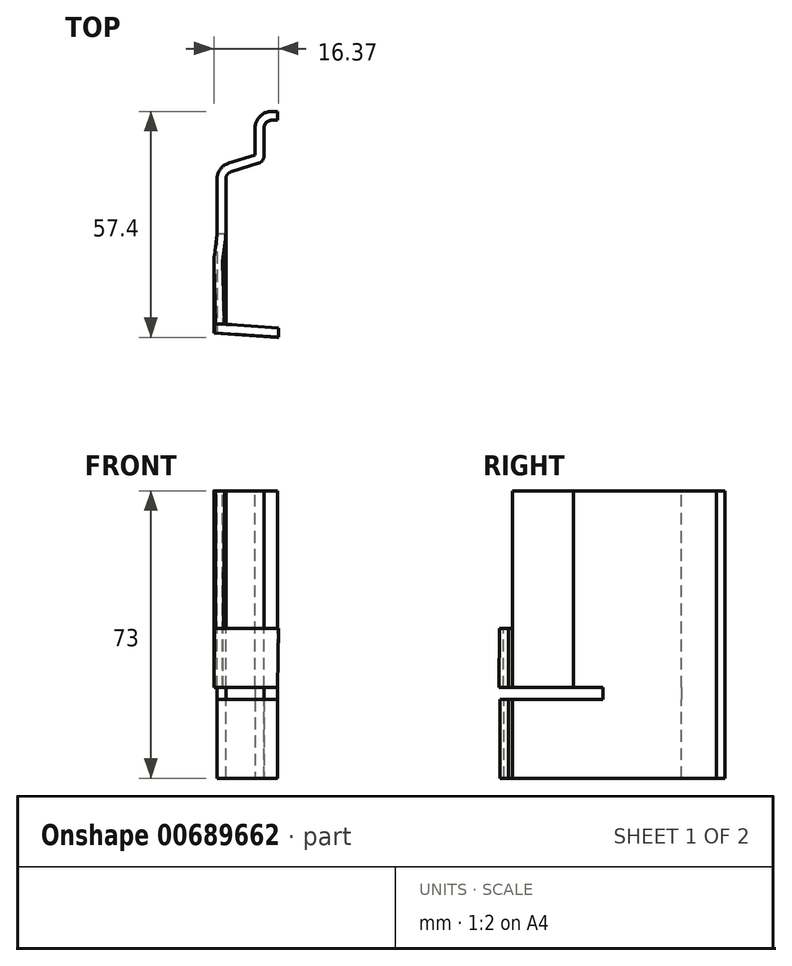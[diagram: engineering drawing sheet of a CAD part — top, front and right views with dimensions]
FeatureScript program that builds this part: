
annotation { "Feature Type Name" : "Feature", "Feature Type Description" : "" }
export const myFeature = defineFeature(function(context is Context, id is Id, definition is map)
    precondition{}
    {
        {
            var Q0;
            Q0=qCreatedBy(makeId("Top.planeOp"),FACE);
            var sketch = newSketch(context, id + "F0", { "sketchPlane" : qUnion([Q0])});
            skLineSegment(sketch, "E0", {"start": v(-3.5, 27.5) * mm, "end": v(-3.5, 20.47) * mm});
            skLineSegment(sketch, "E1", {"start": v(-4.9, 18.56) * mm, "end": v(-11.8, 16.44) * mm});
            skLineSegment(sketch, "E2", {"start": v(-13.2, 14.53) * mm, "end": v(-13.2, 0.66) * mm});
            skLineSegment(sketch, "E3", {"start": v(-13.29, -0.66) * mm, "end": v(-13.9, -5.19) * mm});
            skLineSegment(sketch, "E4", {"start": v(-13.97, -6.82) * mm, "end": v(-13.5, -22.25) * mm});
            skLineSegment(sketch, "E5", {"start": v(-1.5, 29.5) * mm, "end": v(0, 29.5) * mm});
            skPoint(sketch, "E6.visualSharp", {"position": v(-13.2, 16) * mm});
            skArc(sketch, "E6.filletArc", {"start": v(-11.8, 16.44) * mm, "mid": v(-12.8, 15.71) * mm, "end": v(-13.2, 14.53) * mm});
            skPoint(sketch, "E7.visualSharp", {"position": v(-3.5, 19) * mm});
            skArc(sketch, "E7.filletArc", {"start": v(-4.9, 18.56) * mm, "mid": v(-3.9, 19.29) * mm, "end": v(-3.5, 20.47) * mm});
            skPoint(sketch, "E8.visualSharp", {"position": v(-3.5, 29.5) * mm});
            skArc(sketch, "E8.filletArc", {"start": v(-1.5, 29.5) * mm, "mid": v(-2.91, 28.91) * mm, "end": v(-3.5, 27.5) * mm});
            skPoint(sketch, "E9.visualSharp", {"position": v(-13.2, 0) * mm});
            skArc(sketch, "E9.filletArc", {"start": v(-13.29, -0.66) * mm, "mid": v(-13.22, 0) * mm, "end": v(-13.2, 0.66) * mm});
            skPoint(sketch, "E10.visualSharp", {"position": v(-14, -6) * mm});
            skArc(sketch, "E10.filletArc", {"start": v(-13.9, -5.19) * mm, "mid": v(-13.97, -6) * mm, "end": v(-13.97, -6.82) * mm});
            skLineSegment(sketch, "E11.0", {"start": v(-16.22, -6.89) * mm, "end": v(-15.75, -22.32) * mm});
            skArc(sketch, "E11.1", {"start": v(-16.12, -4.9) * mm, "mid": v(-16.21, -5.89) * mm, "end": v(-16.22, -6.89) * mm});
            skLineSegment(sketch, "E11.2", {"start": v(-15.52, -0.36) * mm, "end": v(-16.12, -4.9) * mm});
            skArc(sketch, "E11.3", {"start": v(-15.52, -0.36) * mm, "mid": v(-15.47, 0.15) * mm, "end": v(-15.45, 0.66) * mm});
            skLineSegment(sketch, "E11.4", {"start": v(-15.45, 14.53) * mm, "end": v(-15.45, 0.66) * mm});
            skArc(sketch, "E11.5", {"start": v(-12.46, 18.59) * mm, "mid": v(-14.62, 17.05) * mm, "end": v(-15.45, 14.53) * mm});
            skLineSegment(sketch, "E11.6", {"start": v(-1.5, 31.75) * mm, "end": v(0, 31.75) * mm});
            skArc(sketch, "E11.7", {"start": v(-1.5, 31.75) * mm, "mid": v(-4.5, 30.5) * mm, "end": v(-5.75, 27.5) * mm});
            skLineSegment(sketch, "E11.8", {"start": v(-5.75, 27.5) * mm, "end": v(-5.75, 20.66) * mm});
            skLineSegment(sketch, "E11.9", {"start": v(-5.75, 20.66) * mm, "end": v(-12.46, 18.59) * mm});
            skLineSegment(sketch, "E12", {"start": v(-13.5, -22.25) * mm, "end": v(-15.75, -22.32) * mm});
            skLineSegment(sketch, "E13", {"start": v(0, 29.5) * mm, "end": v(0, 31.75) * mm});
            skSolve(sketch);
        }
        {
            var Q0;
            Q0=qCreatedBy(makeId("Top.planeOp"),FACE);
            cPlane(context, id + "F1", {"entities" : qUnion([Q0]), "cplaneType" : CPlaneType.OFFSET, "offset" : 50 * mm, "oppositeDirection" : true, "width" : 150 * mm, "height" : 150 * mm});
        }
        {
            var Q0;
            Q0=qCreatedBy(id+"F1.planeOp",FACE);
            var sketch = newSketch(context, id + "F2", { "sketchPlane" : qUnion([Q0])});
            skLineSegment(sketch, "E14", {"start": v(-3.5, 27.5) * mm, "end": v(-3.5, 20.47) * mm});
            skLineSegment(sketch, "E15", {"start": v(-4.9, 18.56) * mm, "end": v(-11.8, 16.44) * mm});
            skLineSegment(sketch, "E16", {"start": v(-13.2, 14.53) * mm, "end": v(-13.2, 0.66) * mm});
            skLineSegment(sketch, "E17", {"start": v(-13.29, -0.66) * mm, "end": v(-13.9, -5.19) * mm});
            skLineSegment(sketch, "E18", {"start": v(-1.5, 29.5) * mm, "end": v(0, 29.5) * mm});
            skPoint(sketch, "E19.visualSharp", {"position": v(-13.2, 16) * mm});
            skArc(sketch, "E19.filletArc", {"start": v(-11.8, 16.44) * mm, "mid": v(-12.8, 15.71) * mm, "end": v(-13.2, 14.53) * mm});
            skPoint(sketch, "E20.visualSharp", {"position": v(-3.5, 19) * mm});
            skArc(sketch, "E20.filletArc", {"start": v(-4.9, 18.56) * mm, "mid": v(-3.9, 19.29) * mm, "end": v(-3.5, 20.47) * mm});
            skPoint(sketch, "E21.visualSharp", {"position": v(-3.5, 29.5) * mm});
            skArc(sketch, "E21.filletArc", {"start": v(-1.5, 29.5) * mm, "mid": v(-2.91, 28.91) * mm, "end": v(-3.5, 27.5) * mm});
            skPoint(sketch, "E22.visualSharp", {"position": v(-13.2, 0) * mm});
            skArc(sketch, "E22.filletArc", {"start": v(-13.29, -0.66) * mm, "mid": v(-13.22, 0) * mm, "end": v(-13.2, 0.66) * mm});
            skPoint(sketch, "E23.visualSharp", {"position": v(-14, -6) * mm});
            skArc(sketch, "E23.filletArc", {"start": v(-13.9, -5.19) * mm, "mid": v(-13.97, -6) * mm, "end": v(-13.97, -6.82) * mm});
            skArc(sketch, "E24.1", {"start": v(-16.12, -4.9) * mm, "mid": v(-16.21, -5.89) * mm, "end": v(-16.22, -6.89) * mm});
            skLineSegment(sketch, "E24.2", {"start": v(-15.52, -0.36) * mm, "end": v(-16.12, -4.9) * mm});
            skArc(sketch, "E24.3", {"start": v(-15.52, -0.36) * mm, "mid": v(-15.47, 0.15) * mm, "end": v(-15.45, 0.66) * mm});
            skLineSegment(sketch, "E24.4", {"start": v(-15.45, 14.53) * mm, "end": v(-15.45, 0.66) * mm});
            skArc(sketch, "E24.5", {"start": v(-12.46, 18.59) * mm, "mid": v(-14.62, 17.05) * mm, "end": v(-15.45, 14.53) * mm});
            skLineSegment(sketch, "E24.6", {"start": v(-1.5, 31.75) * mm, "end": v(0, 31.75) * mm});
            skArc(sketch, "E24.7", {"start": v(-1.5, 31.75) * mm, "mid": v(-4.5, 30.5) * mm, "end": v(-5.75, 27.5) * mm});
            skLineSegment(sketch, "E24.8", {"start": v(-5.75, 27.5) * mm, "end": v(-5.75, 20.66) * mm});
            skLineSegment(sketch, "E24.9", {"start": v(-5.75, 20.66) * mm, "end": v(-12.46, 18.59) * mm});
            skLineSegment(sketch, "E25", {"start": v(0, 29.5) * mm, "end": v(0, 31.75) * mm});
            skLineSegment(sketch, "E26", {"start": v(-13.97, -6.82) * mm, "end": v(-13.97, -22.32) * mm});
            skLineSegment(sketch, "E27", {"start": v(-16.22, -6.89) * mm, "end": v(-16.22, -22.32) * mm});
            skLineSegment(sketch, "E28", {"start": v(-16.22, -22.32) * mm, "end": v(-13.97, -22.32) * mm});
            skSolve(sketch);
        }
        {
            var Q0;
            Q0=makeQuery(id+"F2.imprint","IMPRINT",FACE,{"disambiguationData":[TD([[makeQuery(id+"F2.imprint","IMPRINT",EDGE,{"derivedFrom":sQuery(id+"F2.wireOp",EDGE,"E14")}),-1.0]])]});
            var Q1;
            Q1=makeQuery(id+"F0.imprint","IMPRINT",FACE,{"disambiguationData":[TD([[makeQuery(id+"F0.imprint","IMPRINT",EDGE,{"derivedFrom":sQuery(id+"F0.wireOp",EDGE,"E0")}),-1.0]])]});
            loft(context, id + "F3", {"sheetProfilesArray" : [{ "sheetProfileEntities" : qUnion([Q0]) }, { "sheetProfileEntities" : qUnion([Q1]) }]});
        }
        {
            var Q0;
            Q0=makeQuery(id+"F3.opLoft","CAP_FACE",FACE,{"disambiguationData":[OSD([makeQuery(id+"F2.imprint","IMPRINT",FACE,{"disambiguationData":[TD([[makeQuery(id+"F2.imprint","IMPRINT",EDGE,{"derivedFrom":sQuery(id+"F2.wireOp",EDGE,"E14")}),-1.0]])]})])],"isStart":true});
            var sketch = newSketch(context, id + "F4", { "sketchPlane" : qUnion([Q0])});
            skLineSegment(sketch, "E29", {"start": v(-15.45, -0.66) * mm, "end": v(-13.2, -0.66) * mm});
            skSolve(sketch);
        }
        {
            var Q0;
            Q0=makeQuery(id+"F4.imprint","IMPRINT",FACE,{"disambiguationData":[TD([[makeQuery(id+"F4.imprint","IMPRINT",EDGE,{"derivedFrom":sQuery(id+"F4.wireOp",EDGE,"E29")}),-1.0]])]});
            extrude(context, id + "F5", {"entities" : qUnion([Q0]), "operationType" : NewBodyOperationType.ADD, "depth" : 3 * mm, "offsetDistance" : 25 * mm});
        }
        {
            var Q0;
            Q0=makeQuery(id+"F5.opExtrude","CAP_FACE",FACE,{"disambiguationData":[OSD([sQuery(id+"F2.wireOp",EDGE,"E14"),sQuery(id+"F2.wireOp",EDGE,"E15"),sQuery(id+"F2.wireOp",EDGE,"E16"),sQuery(id+"F2.wireOp",EDGE,"E18"),sQuery(id+"F2.wireOp",EDGE,"E19.filletArc"),sQuery(id+"F2.wireOp",EDGE,"E20.filletArc"),sQuery(id+"F2.wireOp",EDGE,"E21.filletArc"),sQuery(id+"F2.wireOp",EDGE,"E22.filletArc"),sQuery(id+"F2.wireOp",EDGE,"E24.3"),sQuery(id+"F2.wireOp",EDGE,"E24.4"),sQuery(id+"F2.wireOp",EDGE,"E24.5"),sQuery(id+"F2.wireOp",EDGE,"E24.6"),sQuery(id+"F2.wireOp",EDGE,"E24.7"),sQuery(id+"F2.wireOp",EDGE,"E24.8"),sQuery(id+"F2.wireOp",EDGE,"E24.9"),sQuery(id+"F2.wireOp",EDGE,"E25"),sQuery(id+"F4.wireOp",EDGE,"E29")])],"isStart":false});
            var sketch = newSketch(context, id + "F6", { "sketchPlane" : qUnion([Q0])});
            skLineSegment(sketch, "E30", {"start": v(-13.2, -0.66) * mm, "end": v(-13.2, 22.34) * mm});
            skLineSegment(sketch, "E31", {"start": v(-13.2, 22.34) * mm, "end": v(-15.45, 22.34) * mm});
            skLineSegment(sketch, "E32", {"start": v(-15.45, 22.34) * mm, "end": v(-15.45, -0.66) * mm});
            skSolve(sketch);
        }
        {
            var Q0;
            Q0=makeQuery(id+"F6.imprint","IMPRINT",FACE,{"disambiguationData":[TD([[makeQuery(id+"F6.imprint","IMPRINT",EDGE,{"derivedFrom":makeQuery(id+"F5.opExtrude","CAP_EDGE",EDGE,{"disambiguationData":[OSD([sQuery(id+"F4.wireOp",EDGE,"E29")])],"isStart":false})}),-1.0]])]});
            var Q1;
            Q1=makeQuery(id+"F6.imprint","IMPRINT",FACE,{"disambiguationData":[TD([[makeQuery(id+"F6.imprint","IMPRINT",EDGE,{"derivedFrom":sQuery(id+"F6.wireOp",EDGE,"E30")}),1.0]])]});
            extrude(context, id + "F7", {"entities" : qUnion([Q0, Q1]), "operationType" : NewBodyOperationType.ADD, "depth" : 20 * mm, "offsetDistance" : 25 * mm});
        }
        {
            var Q0;
            Q0=makeQuery(id+"F7.opExtrude","CAP_FACE",FACE,{"disambiguationData":[OSD([sQuery(id+"F2.wireOp",EDGE,"E14"),sQuery(id+"F2.wireOp",EDGE,"E15"),sQuery(id+"F2.wireOp",EDGE,"E16"),sQuery(id+"F2.wireOp",EDGE,"E18"),sQuery(id+"F2.wireOp",EDGE,"E19.filletArc"),sQuery(id+"F2.wireOp",EDGE,"E20.filletArc"),sQuery(id+"F2.wireOp",EDGE,"E21.filletArc"),sQuery(id+"F2.wireOp",EDGE,"E22.filletArc"),sQuery(id+"F2.wireOp",EDGE,"E24.3"),sQuery(id+"F2.wireOp",EDGE,"E24.4"),sQuery(id+"F2.wireOp",EDGE,"E24.5"),sQuery(id+"F2.wireOp",EDGE,"E24.6"),sQuery(id+"F2.wireOp",EDGE,"E24.7"),sQuery(id+"F2.wireOp",EDGE,"E24.8"),sQuery(id+"F2.wireOp",EDGE,"E24.9"),sQuery(id+"F2.wireOp",EDGE,"E25"),sQuery(id+"F6.wireOp",EDGE,"E30"),sQuery(id+"F6.wireOp",EDGE,"E31"),sQuery(id+"F6.wireOp",EDGE,"E32")])],"isStart":false});
            var sketch = newSketch(context, id + "F8", { "sketchPlane" : qUnion([Q0])});
            skLineSegment(sketch, "E33", {"start": v(-13.2, 22.34) * mm, "end": v(0, 23.25) * mm});
            skLineSegment(sketch, "E34", {"start": v(0, 23.25) * mm, "end": v(0, 25.5) * mm});
            skLineSegment(sketch, "E35", {"start": v(0, 25.5) * mm, "end": v(-15.45, 24.43) * mm});
            skLineSegment(sketch, "E36", {"start": v(-15.45, 24.43) * mm, "end": v(-15.45, 22.34) * mm});
            skSolve(sketch);
        }
        {
            var Q0;
            Q0=makeQuery(id+"F3.opLoft","CAP_FACE",FACE,{"disambiguationData":[OSD([makeQuery(id+"F2.imprint","IMPRINT",FACE,{"disambiguationData":[TD([[makeQuery(id+"F2.imprint","IMPRINT",EDGE,{"derivedFrom":sQuery(id+"F2.wireOp",EDGE,"E14")}),-1.0]])]})])],"isStart":true});
            var sketch = newSketch(context, id + "F9", { "sketchPlane" : qUnion([Q0])});
            skLineSegment(sketch, "E37", {"start": v(-13.97, 22.32) * mm, "end": v(0, 23.25) * mm});
            skLineSegment(sketch, "E38", {"start": v(0, 23.25) * mm, "end": v(0, 25.65) * mm});
            skLineSegment(sketch, "E39", {"start": v(0, 25.65) * mm, "end": v(-16.22, 24.57) * mm});
            skLineSegment(sketch, "E40", {"start": v(-16.22, 24.57) * mm, "end": v(-16.22, 22.32) * mm});
            skSolve(sketch);
        }
        {
            var Q0;
            Q0=makeQuery(id+"F8.imprint","IMPRINT",FACE,{"disambiguationData":[TD([[makeQuery(id+"F8.imprint","IMPRINT",EDGE,{"derivedFrom":sQuery(id+"F8.wireOp",EDGE,"E33")}),1.0]])]});
            var Q1;
            Q1=makeQuery(id+"F7.opExtrude","SWEPT_EDGE",EDGE,{"disambiguationData":[OSD([sQuery(id+"F6.wireOp",EDGE,"E31"),sQuery(id+"F6.wireOp",EDGE,"E32")])]});
            sweep(context, id + "F10", {"operationType" : NewBodyOperationType.ADD, "profiles" : qUnion([Q0]), "path" : qUnion([Q1])});
        }
        {
            var Q0;
            Q0=makeQuery(id+"F9.imprint","IMPRINT",FACE,{"disambiguationData":[TD([[makeQuery(id+"F9.imprint","IMPRINT",EDGE,{"derivedFrom":sQuery(id+"F9.wireOp",EDGE,"E37")}),1.0]])]});
            var Q1;
            Q1=makeQuery(id+"F3.opLoft","SWEPT_EDGE",EDGE,{"disambiguationData":[OSD([sQuery(id+"F0.wireOp",EDGE,"E4"),sQuery(id+"F0.wireOp",EDGE,"E12"),sQuery(id+"F2.wireOp",EDGE,"E26"),sQuery(id+"F2.wireOp",EDGE,"E28")])]});
            sweep(context, id + "F11", {"operationType" : NewBodyOperationType.ADD, "profiles" : qUnion([Q0]), "path" : qUnion([Q1])});
        }
        {
            var Q0;
            {var subQ0=sQuery(id+"F0.wireOp",EDGE,"E12");var subQ1=sQuery(id+"F0.wireOp",EDGE,"E4");Q0=makeQuery(id+"F11.boolean.opBoolean","MERGE",FACE,{"derivedFrom":[makeQuery(id+"F3.opLoft","CAP_FACE",FACE,{"disambiguationData":[OSD([makeQuery(id+"F0.imprint","IMPRINT",FACE,{"disambiguationData":[TD([[makeQuery(id+"F0.imprint","IMPRINT",EDGE,{"derivedFrom":sQuery(id+"F0.wireOp",EDGE,"E0")}),-1.0]])]})])],"isStart":true}),makeQuery(id+"F11.opSweep","CAP_FACE",FACE,{"disambiguationData":[OSD([subQ1,subQ0,sQuery(id+"F2.wireOp",EDGE,"E26"),sQuery(id+"F2.wireOp",EDGE,"E27"),sQuery(id+"F2.wireOp",EDGE,"E28"),sQuery(id+"F9.wireOp",EDGE,"E37"),sQuery(id+"F9.wireOp",EDGE,"E38"),sQuery(id+"F9.wireOp",EDGE,"E39"),sQuery(id+"F9.wireOp",EDGE,"E40")])],"isStart":false})]});}
            var sketch = newSketch(context, id + "F12", { "sketchPlane" : qUnion([Q0])});
            skLineSegment(sketch, "E41", {"start": v(-13.5, -22.25) * mm, "end": v(-15.75, -22.32) * mm});
            skLineSegment(sketch, "E42", {"start": v(-15.75, -22.32) * mm, "end": v(-16.85, -22.32) * mm});
            skLineSegment(sketch, "E43", {"start": v(-16.85, -22.32) * mm, "end": v(-16.85, -25.57) * mm});
            skLineSegment(sketch, "E44", {"start": v(-16.85, -25.57) * mm, "end": v(1.48, -27.05) * mm});
            skLineSegment(sketch, "E45", {"start": v(1.48, -27.05) * mm, "end": v(1.48, -22.32) * mm});
            skLineSegment(sketch, "E46", {"start": v(1.48, -22.32) * mm, "end": v(-13.5, -22.25) * mm});
            skSolve(sketch);
        }
        {
            var Q0;
            Q0=makeQuery(id+"F12.imprint","IMPRINT",FACE,{"disambiguationData":[TD([[makeQuery(id+"F12.imprint","IMPRINT",EDGE,{"derivedFrom":sQuery(id+"F12.wireOp",EDGE,"E41")}),1.0]])]});
            var Q1;
            Q1=makeQuery(id+"F12.imprint","IMPRINT",FACE,{"disambiguationData":[TD([[makeQuery(id+"F12.imprint","IMPRINT",EDGE,{"derivedFrom":sQuery(id+"F12.wireOp",EDGE,"E42")}),1.0]])]});
            extrude(context, id + "F13", {"entities" : qUnion([Q0, Q1]), "operationType" : NewBodyOperationType.REMOVE, "oppositeDirection" : true, "depth" : 35 * mm, "offsetDistance" : 25 * mm});
        }
    });
